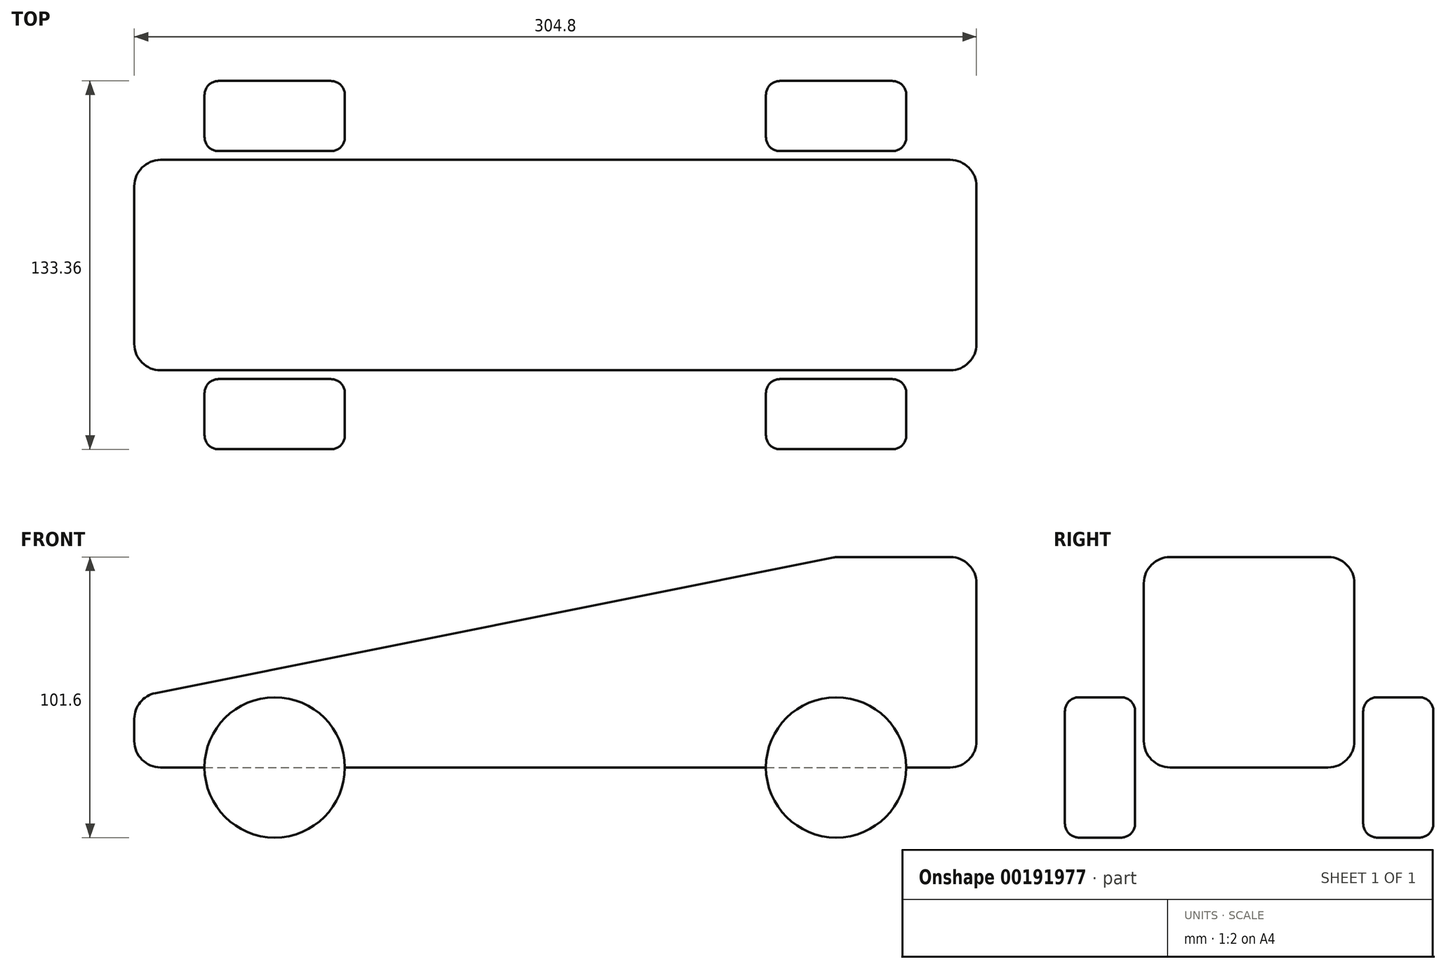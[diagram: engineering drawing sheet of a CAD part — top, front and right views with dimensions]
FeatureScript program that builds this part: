
annotation { "Feature Type Name" : "Feature", "Feature Type Description" : "" }
export const myFeature = defineFeature(function(context is Context, id is Id, definition is map)
    precondition{}
    {
        {
            var Q0;
            Q0=qCreatedBy(makeId("Front.planeOp"),FACE);
            var sketch = newSketch(context, id + "F0", { "sketchPlane" : qUnion([Q0])});
            skLineSegment(sketch, "E0", {"start": v(-152.4, 0) * mm, "end": v(152.4, 0) * mm});
            skLineSegment(sketch, "E1", {"start": v(152.4, 0) * mm, "end": v(152.4, 76.2) * mm});
            skLineSegment(sketch, "E2", {"start": v(-152.4, 0) * mm, "end": v(-152.4, 25.4) * mm});
            skLineSegment(sketch, "E3", {"start": v(152.4, 76.2) * mm, "end": v(101.6, 76.2) * mm});
            skLineSegment(sketch, "E4", {"start": v(101.6, 76.2) * mm, "end": v(-152.4, 25.4) * mm});
            skPoint(sketch, "E5", {"position": v(0, 0) * mm});
            skSolve(sketch);
        }
        {
            var Q0;
            Q0=makeQuery(id+"F0.imprint","IMPRINT",FACE,{"disambiguationData":[TD([[makeQuery(id+"F0.imprint","IMPRINT",EDGE,{"derivedFrom":sQuery(id+"F0.wireOp",EDGE,"E0")}),1.0]])]});
            extrude(context, id + "F1", {"entities" : qUnion([Q0]), "depth" : 76.2 * mm, "symmetric" : true});
        }
        {
            var Q0;
            Q0=makeQuery(id+"F1.opExtrude","CAP_FACE",FACE,{"disambiguationData":[OSD([sQuery(id+"F0.wireOp",EDGE,"E0"),sQuery(id+"F0.wireOp",EDGE,"E1"),sQuery(id+"F0.wireOp",EDGE,"E2"),sQuery(id+"F0.wireOp",EDGE,"E3"),sQuery(id+"F0.wireOp",EDGE,"E4")])],"isStart":false});
            cPlane(context, id + "F2", {"entities" : qUnion([Q0]), "cplaneType" : CPlaneType.OFFSET, "offset" : 3.17 * mm, "width" : 152.4 * mm, "height" : 152.4 * mm});
        }
        {
            var Q0;
            Q0=qCreatedBy(id+"F2.planeOp",FACE);
            var sketch = newSketch(context, id + "F3", { "sketchPlane" : qUnion([Q0])});
            skLineSegment(sketch, "E6", {"start": v(-101.6, 0) * mm, "end": v(101.6, 0) * mm, "construction": true});
            skCircle(sketch, "E7", {"center": v(-101.6, 0) * mm, "radius": 25.4 * mm});
            skSolve(sketch);
        }
        {
            var Q0;
            Q0 = qSketchRegion(id + "F3", true);
            extrude(context, id + "F4", {"entities" : qUnion([Q0]), "depth" : 25.4 * mm});
        }
        {
            var Q0;
            Q0=makeQuery(id+"F4.opExtrude","CAP_EDGE",EDGE,{"disambiguationData":[OSD([sQuery(id+"F3.wireOp",EDGE,"E7")])],"isStart":false});
            var Q1;
            Q1=makeQuery(id+"F4.opExtrude","CAP_EDGE",EDGE,{"disambiguationData":[OSD([sQuery(id+"F3.wireOp",EDGE,"E7")])],"isStart":true});
            fillet(context, id + "F5", {"entities" : qUnion([Q0, Q1]), "radius" : 5.08 * mm, "tangentPropagation" : true, "allowEdgeOverflow" : false});
        }
        {
            var Q0;
            Q0=makeQuery(id+"F4.opExtrude","SWEPT_BODY",BODY,{"disambiguationData":[OSD([sQuery(id+"F3.wireOp",EDGE,"E7")])]});
            var Q1;
            Q1=qCreatedBy(makeId("Right.planeOp"),FACE);
            mirror(context, id + "F6", {"entities" : qUnion([Q0]), "mirrorPlane" : qUnion([Q1])});
        }
        {
            var Q0;
            Q0=makeQuery(id+"F4.opExtrude","SWEPT_BODY",BODY,{"disambiguationData":[OSD([sQuery(id+"F3.wireOp",EDGE,"E7")])]});
            var Q1;
            Q1=makeQuery(id+"F6.opPattern","COPY",BODY,{"derivedFrom":makeQuery(id+"F4.opExtrude","SWEPT_BODY",BODY,{"disambiguationData":[OSD([sQuery(id+"F3.wireOp",EDGE,"E7")])]}),"instanceName":"1"});
            var Q2;
            Q2=qCreatedBy(makeId("Front.planeOp"),FACE);
            mirror(context, id + "F7", {"entities" : qUnion([Q0, Q1]), "mirrorPlane" : qUnion([Q2])});
        }
        {
            var Q0;
            Q0=makeQuery(id+"F1.opExtrude","SWEPT_FACE",FACE,{"disambiguationData":[OSD([sQuery(id+"F0.wireOp",EDGE,"E4")])]});
            var Q1;
            Q1=makeQuery(id+"F1.opExtrude","SWEPT_FACE",FACE,{"disambiguationData":[OSD([sQuery(id+"F0.wireOp",EDGE,"E3")])]});
            var Q2;
            Q2=makeQuery(id+"F1.opExtrude","SWEPT_FACE",FACE,{"disambiguationData":[OSD([sQuery(id+"F0.wireOp",EDGE,"E1")])]});
            var Q3;
            Q3=makeQuery(id+"F1.opExtrude","CAP_FACE",FACE,{"disambiguationData":[OSD([sQuery(id+"F0.wireOp",EDGE,"E0"),sQuery(id+"F0.wireOp",EDGE,"E1"),sQuery(id+"F0.wireOp",EDGE,"E2"),sQuery(id+"F0.wireOp",EDGE,"E3"),sQuery(id+"F0.wireOp",EDGE,"E4")])],"isStart":false});
            var Q4;
            Q4=makeQuery(id+"F1.opExtrude","CAP_FACE",FACE,{"disambiguationData":[OSD([sQuery(id+"F0.wireOp",EDGE,"E0"),sQuery(id+"F0.wireOp",EDGE,"E1"),sQuery(id+"F0.wireOp",EDGE,"E2"),sQuery(id+"F0.wireOp",EDGE,"E3"),sQuery(id+"F0.wireOp",EDGE,"E4")])],"isStart":true});
            var Q5;
            Q5=makeQuery(id+"F1.opExtrude","SWEPT_EDGE",EDGE,{"disambiguationData":[OSD([sQuery(id+"F0.wireOp",EDGE,"E0"),sQuery(id+"F0.wireOp",EDGE,"E2")])]});
            fillet(context, id + "F8", {"entities" : qUnion([Q0, Q1, Q2, Q3, Q4, Q5]), "radius" : 9.52 * mm, "tangentPropagation" : true, "allowEdgeOverflow" : false});
        }
    });
